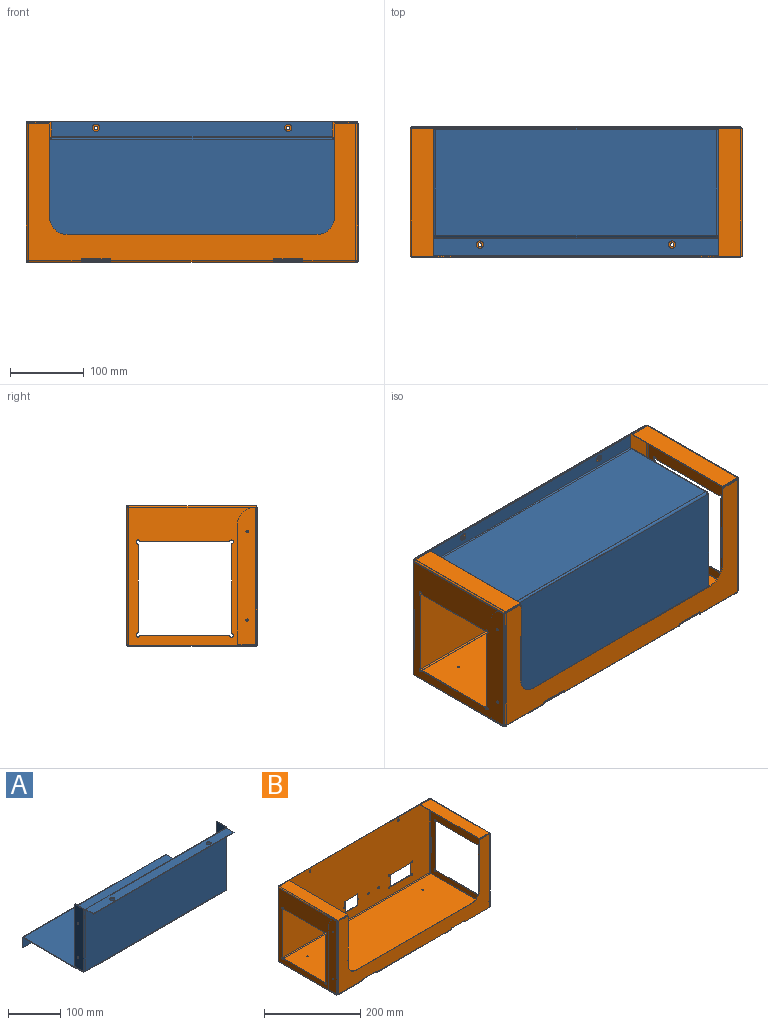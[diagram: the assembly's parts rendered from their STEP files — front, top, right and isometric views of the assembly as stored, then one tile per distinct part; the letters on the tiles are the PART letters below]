
ASSEMBLY  parts=2 mates=1
PART A: 60 faces, bbox 386x189.5x173 mm
  f0: plane 1.5x1.5mm, normal (0,-1,0), area 2.3mm2, adj f5,f6,f7,f45
  f1: plane 1.5x1.5mm, normal (0,-1,0), area 2.3mm2, adj f2,f6,f7,f46
  f2: plane 1.5x1.5mm, normal (0,-1,0), area 2.3mm2, adj f1,f3,f6,f7
  f3: plane 162x1.5mm, normal (-1,0,0), area 243mm2, adj f2,f6,f7,f56
  f4: plane 162x1.5mm, normal (1,0,0), area 243mm2, adj f5,f6,f7,f57
  f5: plane 1.5x1.5mm, normal (0,-1,0), area 2.3mm2, adj f0,f4,f6,f7
  f6: plane 386x162mm, normal (0,0,-1), area 62532mm2, adj f0,f1,f2,f3,f4,f5,f47,f59
  f7: plane 386x162mm, normal (0,0,1), area 62532mm2, adj f0,f1,f2,f3,f4,f5,f48,f58
  f8: plane 380x142.5mm, normal (0,-1,0), area 54150mm2, adj f20,f32,f44,f47
  f9: plane 380x142.5mm, normal (0,1,0), area 54150mm2, adj f21,f33,f43,f48
  f10: plane 145.5x1.5mm, normal (0,1,0), area 218.3mm2, adj f11,f15,f16,f17
  f11: plane 23x1.5mm, normal (0,0,-1), area 34.5mm2, adj f10,f16,f17,f18
  f12: plane 3x1.5mm, normal (0,-1,0), area 4.5mm2, adj f15,f16,f17,f19
  f13: cylinder r=2.25mm len=4.5mm, axis (-1,0,0), area 21.2mm2, adj f16,f17
  f14: cylinder r=2.25mm len=4.5mm, axis (-1,0,0), area 21.2mm2, adj f16,f17
  f15: plane 23x1.5mm, normal (0,0,1), area 34.5mm2, adj f10,f12,f16,f17
  f16: plane 145.5x23mm, normal (-1,0,0), area 3314.7mm2, adj f10,f11,f12,f13,f14,f15,f20
  f17: plane 145.5x23mm, normal (1,0,0), area 3314.7mm2, adj f10,f11,f12,f13,f14,f15,f21
  f18: plane 3x3mm, normal (0,0,-1), area 5.3mm2, adj f11,f20,f21,f46
  f19: plane 3x3mm, normal (0,0,1), area 5.3mm2, adj f12,f20,f21,f41
  f20: cylinder r=3mm len=142.5mm, axis (0,0,-1), area 671.5mm2, adj f8,f16,f18,f19
  f21: cylinder r=1.5mm len=142.5mm, axis (0,0,-1), area 335.8mm2, adj f9,f17,f18,f19
  f22: plane 3x1.5mm, normal (0,-1,0), area 4.5mm2, adj f24,f28,f29,f30
  f23: plane 145.5x1.5mm, normal (0,1,0), area 218.3mm2, adj f24,f27,f28,f29
  f24: plane 23x1.5mm, normal (0,0,1), area 34.5mm2, adj f22,f23,f28,f29
  f25: cylinder r=2.25mm len=4.5mm, axis (1,0,0), area 21.2mm2, adj f28,f29
  f26: cylinder r=2.25mm len=4.5mm, axis (1,0,0), area 21.2mm2, adj f28,f29
  f27: plane 23x1.5mm, normal (0,0,-1), area 34.5mm2, adj f23,f28,f29,f31
  f28: plane 145.5x23mm, normal (1,0,0), area 3314.7mm2, adj f22,f23,f24,f25,f26,f27,f32
  f29: plane 145.5x23mm, normal (-1,0,0), area 3314.7mm2, adj f22,f23,f24,f25,f26,f27,f33
  f30: plane 3x3mm, normal (0,0,1), area 5.3mm2, adj f22,f32,f33,f42
  f31: plane 3x3mm, normal (0,0,-1), area 5.3mm2, adj f27,f32,f33,f45
  f32: cylinder r=3mm len=142.5mm, axis (0,0,1), area 671.5mm2, adj f8,f28,f30,f31
  f33: cylinder r=1.5mm len=142.5mm, axis (0,0,1), area 335.8mm2, adj f9,f29,f30,f31
  f34: plane 380x1.5mm, normal (0,-1,0), area 570mm2, adj f35,f38,f39,f40
  f35: plane 20x1.5mm, normal (-1,0,0), area 30mm2, adj f34,f39,f40,f41
  f36: cylinder r=5mm len=10mm, axis (0,0,-1), area 47.1mm2, adj f39,f40
  f37: cylinder r=5mm len=10mm, axis (0,0,-1), area 47.1mm2, adj f39,f40
  f38: plane 20x1.5mm, normal (1,0,0), area 30mm2, adj f34,f39,f40,f42
  f39: plane 380x20mm, normal (0,0,-1), area 7442.9mm2, adj f34,f35,f36,f37,f38,f44
  f40: plane 380x20mm, normal (0,0,1), area 7442.9mm2, adj f34,f35,f36,f37,f38,f43
  f41: plane 3x3mm, normal (-1,0,0), area 5.3mm2, adj f19,f35,f43,f44
  f42: plane 3x3mm, normal (1,0,0), area 5.3mm2, adj f30,f38,f43,f44
  f43: cylinder r=3mm len=380mm, axis (-1,0,0), area 1790.7mm2, adj f9,f40,f41,f42
  f44: cylinder r=1.5mm len=380mm, axis (-1,0,0), area 895.4mm2, adj f8,f39,f41,f42
  f45: plane 3x3mm, normal (1,0,0), area 5.3mm2, adj f0,f31,f47,f48
  f46: plane 3x3mm, normal (-1,0,0), area 5.3mm2, adj f1,f18,f47,f48
  f47: cylinder r=3mm len=380mm, axis (1,0,0), area 1790.7mm2, adj f6,f8,f45,f46
  f48: cylinder r=1.5mm len=380mm, axis (1,0,0), area 895.4mm2, adj f7,f9,f45,f46
  f49: plane 386x1.5mm, normal (0,0,-1), area 579mm2, adj f50,f53,f54,f55
  f50: plane 23x1.5mm, normal (1,0,0), area 34.5mm2, adj f49,f54,f55,f57
  f51: cylinder r=5mm len=10mm, axis (0,-1,0), area 47.1mm2, adj f54,f55
  f52: cylinder r=5mm len=10mm, axis (0,-1,0), area 47.1mm2, adj f54,f55
  f53: plane 23x1.5mm, normal (-1,0,0), area 34.5mm2, adj f49,f54,f55,f56
  f54: plane 386x23mm, normal (0,-1,0), area 8720.9mm2, adj f49,f50,f51,f52,f53,f59
  f55: plane 386x23mm, normal (0,1,0), area 8720.9mm2, adj f49,f50,f51,f52,f53,f58
  f56: plane 3x3mm, normal (-1,0,0), area 5.3mm2, adj f3,f53,f58,f59
  f57: plane 3x3mm, normal (1,0,0), area 5.3mm2, adj f4,f50,f58,f59
  f58: cylinder r=3mm len=386mm, axis (-1,0,0), area 1819mm2, adj f7,f55,f56,f57
  f59: cylinder r=1.5mm len=386mm, axis (-1,0,0), area 909.5mm2, adj f6,f54,f56,f57
PART B: 190 faces, bbox 449x176x190.5 mm
  f0: plane 1.5x1mm, normal (0,-1,0), area 1.5mm2, adj f6,f20,f21,f187
  f1: plane 1.48x1mm, normal (0,1,0), area 1.5mm2, adj f3,f20,f21,f129
  f2: plane 1x1mm, normal (0,-1,0), area 1mm2, adj f3,f19,f20,f21
  f3: plane 171x1mm, normal (-1,0,0), area 171mm2, adj f1,f2,f20,f21
  f4: plane 1.48x1mm, normal (0,1,0), area 1.5mm2, adj f5,f20,f21,f130
  f5: plane 171x1mm, normal (1,0,0), area 171mm2, adj f4,f6,f20,f21
  f6: plane 1x1mm, normal (0,-1,0), area 1mm2, adj f0,f5,f20,f21
  f7: plane 1x0.5mm, normal (-1,0,0), area 0.5mm2, adj f20,f21,f22,f186
  f8: plane 36x1mm, normal (0,-1,0), area 36mm2, adj f20,f21,f22,f24
  f9: plane 1x0.5mm, normal (1,0,0), area 0.5mm2, adj f20,f21,f24,f183
  f10: plane 1x0.5mm, normal (-1,0,0), area 0.5mm2, adj f20,f21,f25,f182
  f11: plane 36x1mm, normal (0,-1,0), area 36mm2, adj f20,f21,f23,f25
  f12: plane 1x0.5mm, normal (1,0,0), area 0.5mm2, adj f20,f21,f23,f179
  f13: cylinder r=1.25mm len=2.5mm, axis (0,0,1), area 7.9mm2, adj f20,f21
  f14: cylinder r=1.25mm len=2.5mm, axis (0,0,1), area 7.9mm2, adj f20,f21
  f15: cylinder r=1.25mm len=2.5mm, axis (0,0,1), area 7.9mm2, adj f20,f21
  f16: cylinder r=1.25mm len=2.5mm, axis (0,0,1), area 7.9mm2, adj f20,f21
  f17: cylinder r=2.5mm len=5mm, axis (0,0,1), area 15.7mm2, adj f20,f21
  f18: cylinder r=2.5mm len=5mm, axis (0,0,1), area 15.7mm2, adj f20,f21
  f19: plane 1.5x1mm, normal (0,-1,0), area 1.5mm2, adj f2,f20,f21,f178
  f20: plane 446.96x171mm, normal (0,0,-1), area 76174.7mm2, adj f0,f1,f2,f3,f4,f5,f6,f7
  f21: plane 446.96x171mm, normal (0,0,1), area 76174.7mm2, adj f0,f1,f2,f3,f4,f5,f6,f7
  f22: cylinder r=2mm len=2mm, axis (0,0,-1), area 3.1mm2, adj f7,f8,f20,f21
  f23: cylinder r=2mm len=2mm, axis (0,0,1), area 3.1mm2, adj f11,f12,f20,f21
  f24: cylinder r=2mm len=2mm, axis (0,0,1), area 3.1mm2, adj f8,f9,f20,f21
  f25: cylinder r=2mm len=2mm, axis (0,0,-1), area 3.1mm2, adj f10,f11,f20,f21
  f26: cylinder r=1mm len=1mm, axis (0,1,0), area 1.6mm2, adj f27,f50,f51,f52
  f27: plane 56x1mm, normal (0,0,-1), area 56mm2, adj f26,f28,f51,f52
  f28: cylinder r=1mm len=1mm, axis (0,1,0), area 1.6mm2, adj f27,f29,f51,f52
  f29: plane 29x1mm, normal (1,0,0), area 29mm2, adj f28,f30,f51,f52
  f30: cylinder r=1mm len=1mm, axis (0,1,0), area 1.6mm2, adj f29,f31,f51,f52
  f31: plane 56x1mm, normal (0,0,1), area 56mm2, adj f30,f32,f51,f52
  f32: cylinder r=1mm len=1mm, axis (0,1,0), area 1.6mm2, adj f31,f50,f51,f52
  f33: plane 440x1mm, normal (0,0,1), area 440mm2, adj f51,f52,f53,f54
  f34: plane 1x0.5mm, normal (1,0,0), area 0.5mm2, adj f51,f52,f54,f88
  f35: plane 36.5x1mm, normal (0,0,-1), area 36.5mm2, adj f36,f38,f51,f52
  f36: plane 28.8x1mm, normal (1,0,0), area 28.8mm2, adj f35,f37,f51,f52
  f37: plane 36.5x1mm, normal (0,0,1), area 36.5mm2, adj f36,f38,f51,f52
  f38: plane 28.8x1mm, normal (-1,0,0), area 28.8mm2, adj f35,f37,f51,f52
  f39: cylinder r=1.25mm len=2.5mm, axis (0,1,0), area 7.9mm2, adj f51,f52
  f40: cylinder r=1.25mm len=2.5mm, axis (0,1,0), area 7.9mm2, adj f51,f52
  f41: cylinder r=2.25mm len=4.5mm, axis (0,1,0), area 14.1mm2, adj f51,f52
  f42: cylinder r=2.25mm len=4.5mm, axis (0,1,0), area 14.1mm2, adj f51,f52
  f43: cylinder r=2.25mm len=4.5mm, axis (0,1,0), area 14.1mm2, adj f51,f52
  f44: cylinder r=2.25mm len=4.5mm, axis (0,1,0), area 14.1mm2, adj f51,f52
  f45: cylinder r=2.5mm len=5mm, axis (0,1,0), area 15.7mm2, adj f51,f52
  f46: cylinder r=2.5mm len=5mm, axis (0,1,0), area 15.7mm2, adj f51,f52
  f47: cylinder r=2.5mm len=5mm, axis (0,1,0), area 15.7mm2, adj f51,f52
  f48: cylinder r=2.5mm len=5mm, axis (0,1,0), area 15.7mm2, adj f51,f52
  f49: plane 1x0.5mm, normal (-1,0,0), area 0.5mm2, adj f51,f52,f53,f126
  f50: plane 29x1mm, normal (-1,0,0), area 29mm2, adj f26,f32,f51,f52
  f51: plane 444x188mm, normal (0,1,0), area 80470mm2, adj f26,f27,f28,f29,f30,f31,f32,f33
  f52: plane 444x188mm, normal (0,-1,0), area 80470mm2, adj f26,f27,f28,f29,f30,f31,f32,f33
  f53: cylinder r=2mm len=2mm, axis (0,1,0), area 3.1mm2, adj f33,f49,f51,f52
  f54: cylinder r=2mm len=2mm, axis (0,1,0), area 3.1mm2, adj f33,f34,f51,f52
  f55: plane 1.48x1mm, normal (0,1,0), area 1.5mm2, adj f64,f68,f69,f89
  f56: cylinder r=2.5mm len=4.74mm, axis (1,0,0), area 9.5mm2, adj f68,f69,f73,f75
  f57: plane 118.44x1mm, normal (0,1,0), area 118.4mm2, adj f68,f69,f72,f73
  f58: cylinder r=2.5mm len=4.74mm, axis (1,0,0), area 9.5mm2, adj f68,f69,f70,f72
  f59: plane 118.44x1mm, normal (0,0,-1), area 118.4mm2, adj f68,f69,f70,f74
  f60: cylinder r=2.5mm len=4.74mm, axis (1,0,0), area 9.5mm2, adj f68,f69,f74,f78
  f61: plane 118.44x1mm, normal (0,-1,0), area 118.4mm2, adj f68,f69,f77,f78
  f62: cylinder r=2.5mm len=4.74mm, axis (1,0,0), area 9.5mm2, adj f68,f69,f76,f77
  f63: plane 184.98x1mm, normal (0,-1,0), area 185mm2, adj f68,f69,f71,f84
  f64: plane 170.4x1mm, normal (0,0,-1), area 170.4mm2, adj f55,f68,f69,f71
  f65: cylinder r=1.6mm len=3.2mm, axis (1,0,0), area 10.1mm2, adj f68,f69
  f66: cylinder r=1.6mm len=3.2mm, axis (1,0,0), area 10.1mm2, adj f68,f69
  f67: plane 118.44x1mm, normal (0,0,1), area 118.4mm2, adj f68,f69,f75,f76
  f68: plane 186.98x172.4mm, normal (1,0,0), area 16154.3mm2, adj f55,f56,f57,f58,f59,f60,f61,f62
  f69: plane 186.98x172.4mm, normal (-1,0,0), area 16154.3mm2, adj f55,f56,f57,f58,f59,f60,f61,f62
  f70: cylinder r=2mm len=1.79mm, axis (1,0,0), area 2.2mm2, adj f58,f59,f68,f69
  f71: cylinder r=2mm len=2mm, axis (-1,0,0), area 3.1mm2, adj f63,f64,f68,f69
  f72: cylinder r=2mm len=1.79mm, axis (1,0,0), area 2.2mm2, adj f57,f58,f68,f69
  f73: cylinder r=2mm len=1.79mm, axis (1,0,0), area 2.2mm2, adj f56,f57,f68,f69
  f74: cylinder r=2mm len=1.79mm, axis (1,0,0), area 2.2mm2, adj f59,f60,f68,f69
  f75: cylinder r=2mm len=1.79mm, axis (1,0,0), area 2.2mm2, adj f56,f67,f68,f69
  f76: cylinder r=2mm len=1.79mm, axis (1,0,0), area 2.2mm2, adj f62,f67,f68,f69
  f77: cylinder r=2mm len=1.79mm, axis (1,0,0), area 2.2mm2, adj f61,f62,f68,f69
  f78: cylinder r=2mm len=1.79mm, axis (1,0,0), area 2.2mm2, adj f60,f61,f68,f69
  f79: plane 172.4x1mm, normal (-1,0,0), area 172.4mm2, adj f80,f81,f82,f83
  f80: plane 29x1mm, normal (0,-1,0), area 29mm2, adj f79,f82,f83,f84
  f81: plane 29x1mm, normal (0,1,0), area 29mm2, adj f79,f82,f83,f85
  f82: plane 172.4x29mm, normal (0,0,1), area 4999.6mm2, adj f79,f80,f81,f86
  f83: plane 172.4x29mm, normal (0,0,-1), area 4999.6mm2, adj f79,f80,f81,f87
  f84: plane 2.5x2.5mm, normal (0,-1,0), area 3.1mm2, adj f63,f80,f86,f87
  f85: plane 2.5x2.5mm, normal (0,1,0), area 3.1mm2, adj f81,f86,f87,f88
  f86: cylinder r=2.5mm len=172.4mm, axis (0,-1,0), area 677mm2, adj f68,f82,f84,f85
  f87: cylinder r=1.5mm len=172.4mm, axis (0,-1,0), area 406.2mm2, adj f69,f83,f84,f85
  f88: plane 2.5x2.5mm, normal (0,0,1), area 3.1mm2, adj f34,f85,f90,f91
  f89: plane 2.5x2.5mm, normal (0,0,-1), area 3.1mm2, adj f55,f90,f91,f130
  f90: cylinder r=2.5mm len=185.5mm, axis (0,0,1), area 728.5mm2, adj f51,f68,f88,f89
  f91: cylinder r=1.5mm len=185.5mm, axis (0,0,1), area 437.1mm2, adj f52,f69,f88,f89
  f92: cylinder r=2.5mm len=4.74mm, axis (-1,0,0), area 9.5mm2, adj f105,f106,f108,f109
  f93: plane 118.44x1mm, normal (0,-1,0), area 118.4mm2, adj f105,f106,f107,f108
  f94: cylinder r=2.5mm len=4.74mm, axis (-1,0,0), area 9.5mm2, adj f105,f106,f107,f113
  f95: plane 118.44x1mm, normal (0,0,-1), area 118.4mm2, adj f105,f106,f110,f113
  f96: cylinder r=2.5mm len=4.74mm, axis (-1,0,0), area 9.5mm2, adj f105,f106,f110,f111
  f97: plane 118.44x1mm, normal (0,1,0), area 118.4mm2, adj f105,f106,f111,f114
  f98: cylinder r=2.5mm len=4.74mm, axis (-1,0,0), area 9.5mm2, adj f105,f106,f114,f115
  f99: plane 184.98x1mm, normal (0,-1,0), area 185mm2, adj f105,f106,f112,f122
  f100: plane 1.48x1mm, normal (0,1,0), area 1.5mm2, adj f103,f105,f106,f125
  f101: cylinder r=1.6mm len=3.2mm, axis (-1,0,0), area 10.1mm2, adj f105,f106
  f102: cylinder r=1.6mm len=3.2mm, axis (-1,0,0), area 10.1mm2, adj f105,f106
  f103: plane 170.4x1mm, normal (0,0,-1), area 170.4mm2, adj f100,f105,f106,f112
  f104: plane 118.44x1mm, normal (0,0,1), area 118.4mm2, adj f105,f106,f109,f115
  f105: plane 186.98x172.4mm, normal (-1,0,0), area 16154.3mm2, adj f92,f93,f94,f95,f96,f97,f98,f99
  f106: plane 186.98x172.4mm, normal (1,0,0), area 16154.3mm2, adj f92,f93,f94,f95,f96,f97,f98,f99
  f107: cylinder r=2mm len=1.79mm, axis (-1,0,0), area 2.2mm2, adj f93,f94,f105,f106
  f108: cylinder r=2mm len=1.79mm, axis (-1,0,0), area 2.2mm2, adj f92,f93,f105,f106
  f109: cylinder r=2mm len=1.79mm, axis (-1,0,0), area 2.2mm2, adj f92,f104,f105,f106
  f110: cylinder r=2mm len=1.79mm, axis (-1,0,0), area 2.2mm2, adj f95,f96,f105,f106
  f111: cylinder r=2mm len=1.79mm, axis (-1,0,0), area 2.2mm2, adj f96,f97,f105,f106
  f112: cylinder r=2mm len=2mm, axis (1,0,0), area 3.1mm2, adj f99,f103,f105,f106
  f113: cylinder r=2mm len=1.79mm, axis (-1,0,0), area 2.2mm2, adj f94,f95,f105,f106
  f114: cylinder r=2mm len=1.79mm, axis (-1,0,0), area 2.2mm2, adj f97,f98,f105,f106
  f115: cylinder r=2mm len=1.79mm, axis (-1,0,0), area 2.2mm2, adj f98,f104,f105,f106
  f116: plane 172.4x1mm, normal (1,0,0), area 172.4mm2, adj f117,f118,f119,f120
  f117: plane 29x1mm, normal (0,1,0), area 29mm2, adj f116,f119,f120,f121
  f118: plane 29x1mm, normal (0,-1,0), area 29mm2, adj f116,f119,f120,f122
  f119: plane 172.4x29mm, normal (0,0,1), area 4999.6mm2, adj f116,f117,f118,f123
  f120: plane 172.4x29mm, normal (0,0,-1), area 4999.6mm2, adj f116,f117,f118,f124
  f121: plane 2.5x2.5mm, normal (0,1,0), area 3.1mm2, adj f117,f123,f124,f126
  f122: plane 2.5x2.5mm, normal (0,-1,0), area 3.1mm2, adj f99,f118,f123,f124
  f123: cylinder r=2.5mm len=172.4mm, axis (0,1,0), area 677mm2, adj f105,f119,f121,f122
  f124: cylinder r=1.5mm len=172.4mm, axis (0,1,0), area 406.2mm2, adj f106,f120,f121,f122
  f125: plane 2.5x2.5mm, normal (0,0,-1), area 3.1mm2, adj f100,f127,f128,f129
  f126: plane 2.5x2.5mm, normal (0,0,1), area 3.1mm2, adj f49,f121,f127,f128
  f127: cylinder r=2.5mm len=185.5mm, axis (0,0,-1), area 728.5mm2, adj f51,f105,f125,f126
  f128: cylinder r=1.5mm len=185.5mm, axis (0,0,-1), area 437.1mm2, adj f52,f106,f125,f126
  f129: plane 2.5x2.5mm, normal (-1,0,0), area 3.1mm2, adj f1,f125,f131,f132
  f130: plane 2.5x2.5mm, normal (1,0,0), area 3.1mm2, adj f4,f89,f131,f132
  f131: cylinder r=2.5mm len=444mm, axis (-1,0,0), area 1743.6mm2, adj f20,f51,f129,f130
  f132: cylinder r=1.5mm len=444mm, axis (-1,0,0), area 1046.2mm2, adj f21,f52,f129,f130
  f133: plane 1x0.5mm, normal (1,0,0), area 0.5mm2, adj f144,f145,f151,f179
  f134: plane 36x1mm, normal (0,0,-1), area 36mm2, adj f144,f145,f151,f153
  f135: plane 1x0.5mm, normal (-1,0,0), area 0.5mm2, adj f144,f145,f153,f182
  f136: plane 1x0.5mm, normal (1,0,0), area 0.5mm2, adj f144,f145,f152,f183
  f137: plane 36x1mm, normal (0,0,-1), area 36mm2, adj f144,f145,f146,f152
  f138: plane 1x0.5mm, normal (-1,0,0), area 0.5mm2, adj f144,f145,f146,f186
  f139: plane 25.98x1mm, normal (0,0,1), area 26mm2, adj f144,f145,f149,f174
  f140: plane 124x1mm, normal (-1,0,0), area 124mm2, adj f144,f145,f147,f149
  f141: plane 338x1mm, normal (0,0,1), area 338mm2, adj f144,f145,f147,f148
  f142: plane 124x1mm, normal (1,0,0), area 124mm2, adj f144,f145,f148,f150
  f143: plane 25.98x1mm, normal (0,0,1), area 26mm2, adj f144,f145,f150,f163
  f144: plane 441.96x185.5mm, normal (0,-1,0), area 24132.5mm2, adj f133,f134,f135,f136,f137,f138,f139,f140
  f145: plane 441.96x185.5mm, normal (0,1,0), area 24132.5mm2, adj f133,f134,f135,f136,f137,f138,f139,f140
  f146: cylinder r=2mm len=2mm, axis (0,-1,0), area 3.1mm2, adj f137,f138,f144,f145
  f147: cylinder r=24mm len=24mm, axis (0,-1,0), area 37.7mm2, adj f140,f141,f144,f145
  f148: cylinder r=24mm len=24mm, axis (0,1,0), area 37.7mm2, adj f141,f142,f144,f145
  f149: cylinder r=2mm len=2mm, axis (0,1,0), area 3.1mm2, adj f139,f140,f144,f145
  f150: cylinder r=2mm len=2mm, axis (0,-1,0), area 3.1mm2, adj f142,f143,f144,f145
  f151: cylinder r=2mm len=2mm, axis (0,-1,0), area 3.1mm2, adj f133,f134,f144,f145
  f152: cylinder r=2mm len=2mm, axis (0,1,0), area 3.1mm2, adj f136,f137,f144,f145
  f153: cylinder r=2mm len=2mm, axis (0,1,0), area 3.1mm2, adj f134,f135,f144,f145
  f154: plane 159.5x1mm, normal (0,1,0), area 159.5mm2, adj f158,f159,f160,f161
  f155: plane 22x1mm, normal (0,0,-1), area 22mm2, adj f158,f159,f160,f162
  f156: cylinder r=1.25mm len=2.5mm, axis (-1,0,0), area 7.9mm2, adj f158,f159
  f157: cylinder r=1.25mm len=2.5mm, axis (-1,0,0), area 7.9mm2, adj f158,f159
  f158: plane 185.5x24mm, normal (-1,0,0), area 4317.7mm2, adj f154,f155,f156,f157,f160,f161,f164
  f159: plane 185.5x24mm, normal (1,0,0), area 4317.7mm2, adj f154,f155,f156,f157,f160,f161,f165
  f160: cylinder r=2mm len=2mm, axis (-1,0,0), area 3.1mm2, adj f154,f155,f158,f159
  f161: cylinder r=24mm len=24mm, axis (-1,0,0), area 37.7mm2, adj f154,f158,f159,f163
  f162: plane 2.5x2.5mm, normal (0,0,-1), area 3.1mm2, adj f155,f164,f165,f178
  f163: plane 2.5x2.5mm, normal (0,0,1), area 3.1mm2, adj f143,f161,f164,f165
  f164: cylinder r=2.5mm len=185.5mm, axis (0,0,-1), area 728.5mm2, adj f144,f158,f162,f163
  f165: cylinder r=1.5mm len=185.5mm, axis (0,0,-1), area 437.1mm2, adj f145,f159,f162,f163
  f166: plane 159.5x1mm, normal (0,1,0), area 159.5mm2, adj f170,f171,f172,f173
  f167: cylinder r=1.25mm len=2.5mm, axis (1,0,0), area 7.9mm2, adj f170,f171
  f168: cylinder r=1.25mm len=2.5mm, axis (1,0,0), area 7.9mm2, adj f170,f171
  f169: plane 22x1mm, normal (0,0,-1), area 22mm2, adj f170,f171,f172,f175
  f170: plane 185.5x24mm, normal (1,0,0), area 4317.7mm2, adj f166,f167,f168,f169,f172,f173,f176
  f171: plane 185.5x24mm, normal (-1,0,0), area 4317.7mm2, adj f166,f167,f168,f169,f172,f173,f177
  f172: cylinder r=2mm len=2mm, axis (1,0,0), area 3.1mm2, adj f166,f169,f170,f171
  f173: cylinder r=24mm len=24mm, axis (1,0,0), area 37.7mm2, adj f166,f170,f171,f174
  f174: plane 2.5x2.5mm, normal (0,0,1), area 3.1mm2, adj f139,f173,f176,f177
  f175: plane 2.5x2.5mm, normal (0,0,-1), area 3.1mm2, adj f169,f176,f177,f187
  f176: cylinder r=2.5mm len=185.5mm, axis (0,0,1), area 728.5mm2, adj f144,f170,f174,f175
  f177: cylinder r=1.5mm len=185.5mm, axis (0,0,1), area 437.1mm2, adj f145,f171,f174,f175
  f178: plane 2.5x2.5mm, normal (-1,0,0), area 3.1mm2, adj f19,f162,f180,f181
  f179: plane 2.5x2.5mm, normal (1,0,0), area 3.1mm2, adj f12,f133,f180,f181
  f180: cylinder r=2.5mm len=70.98mm, axis (-1,0,0), area 278.7mm2, adj f20,f144,f178,f179
  f181: cylinder r=1.5mm len=70.98mm, axis (-1,0,0), area 167.2mm2, adj f21,f145,f178,f179
  f182: plane 2.5x2.5mm, normal (-1,0,0), area 3.1mm2, adj f10,f135,f184,f185
  f183: plane 2.5x2.5mm, normal (1,0,0), area 3.1mm2, adj f9,f136,f184,f185
  f184: cylinder r=2.5mm len=220mm, axis (-1,0,0), area 863.9mm2, adj f20,f144,f182,f183
  f185: cylinder r=1.5mm len=220mm, axis (-1,0,0), area 518.4mm2, adj f21,f145,f182,f183
  f186: plane 2.5x2.5mm, normal (-1,0,0), area 3.1mm2, adj f7,f138,f188,f189
  f187: plane 2.5x2.5mm, normal (1,0,0), area 3.1mm2, adj f0,f175,f188,f189
  f188: cylinder r=2.5mm len=70.98mm, axis (-1,0,0), area 278.7mm2, adj f20,f144,f186,f187
  f189: cylinder r=1.5mm len=70.98mm, axis (-1,0,0), area 167.2mm2, adj f21,f145,f186,f187
PLACE A rot(axis=(-1,0,0),90deg) t=(0,-61.5,85.75)mm
PLACE B at identity fixed
MATE fastened A.f36 <-> B.f48  axis (0,1,0) through (-130,87,182)mm
